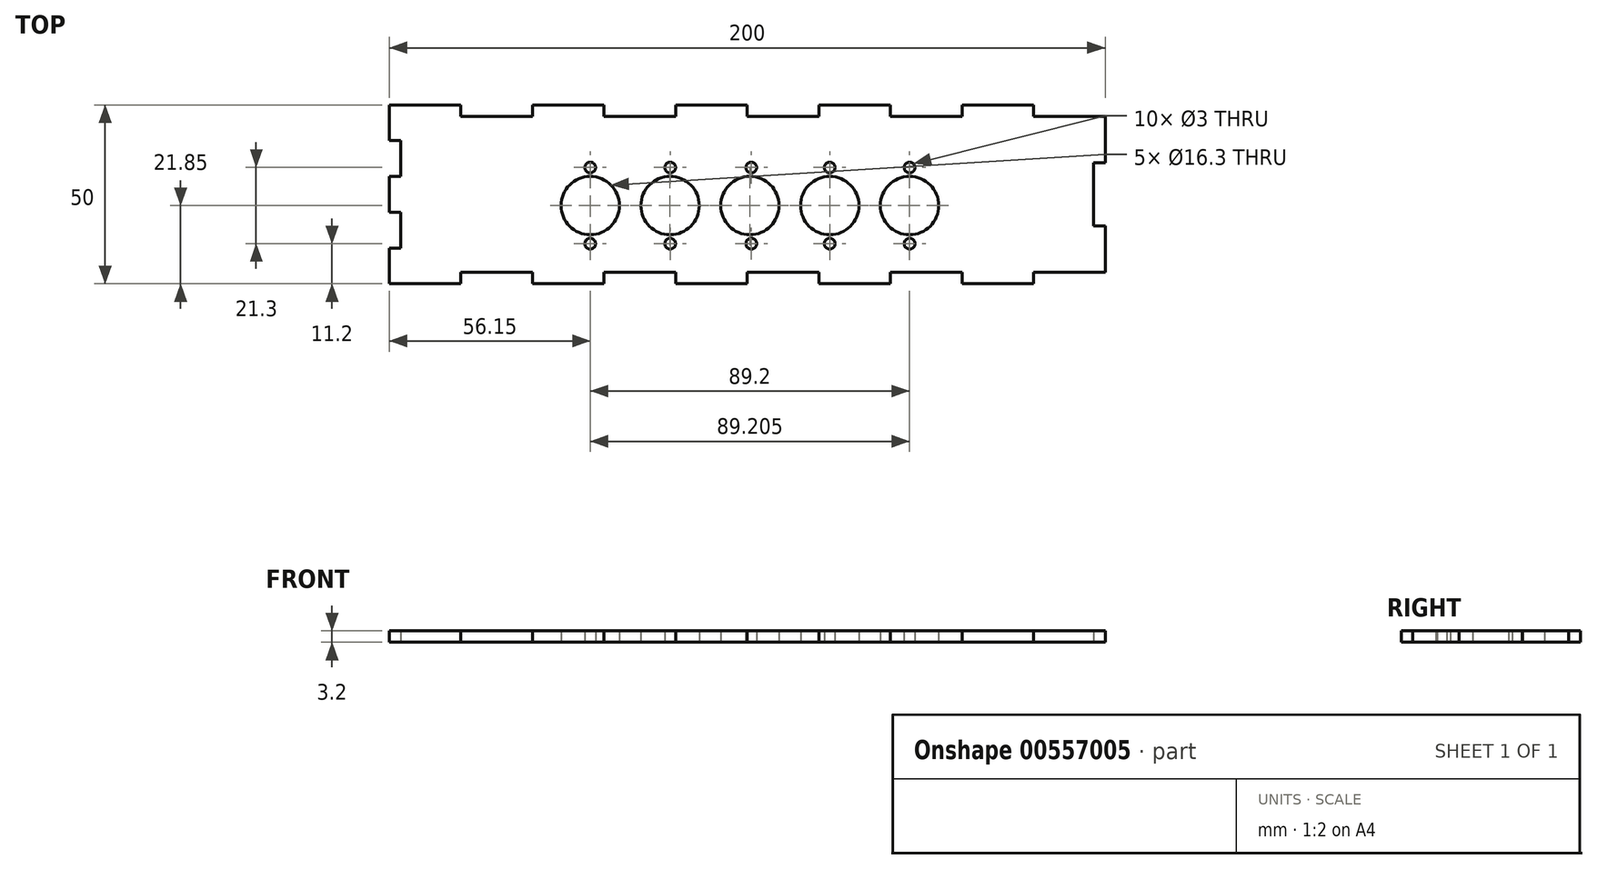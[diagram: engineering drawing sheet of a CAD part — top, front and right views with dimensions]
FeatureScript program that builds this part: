
annotation { "Feature Type Name" : "Feature", "Feature Type Description" : "" }
export const myFeature = defineFeature(function(context is Context, id is Id, definition is map)
    precondition{}
    {
        {
            var Q0;
            Q0=qCreatedBy(makeId("Top.planeOp"),FACE);
            var sketch = newSketch(context, id + "F0", { "sketchPlane" : qUnion([Q0])});
            skLineSegment(sketch, "E0.bottom", {"start": v(-60, 28.15) * mm, "end": v(-40, 28.15) * mm});
            skLineSegment(sketch, "E0.top", {"start": v(-60, -21.85) * mm, "end": v(-40, -21.85) * mm});
            skLineSegment(sketch, "E0.left", {"start": v(-60, 28.15) * mm, "end": v(-60, 18.15) * mm});
            skLineSegment(sketch, "E0.right", {"start": v(140, 24.95) * mm, "end": v(140, 11.95) * mm});
            skCircle(sketch, "E1", {"center": v(-3.85, 0) * mm, "radius": 8.15 * mm});
            skCircle(sketch, "E2", {"center": v(18.45, 0) * mm, "radius": 8.15 * mm});
            skCircle(sketch, "E3", {"center": v(40.75, 0) * mm, "radius": 8.15 * mm});
            skCircle(sketch, "E4", {"center": v(63.05, 0) * mm, "radius": 8.15 * mm});
            skCircle(sketch, "E5", {"center": v(85.35, 0) * mm, "radius": 8.15 * mm});
            skLineSegment(sketch, "E6.top", {"start": v(120, 24.95) * mm, "end": v(140, 24.95) * mm});
            skLineSegment(sketch, "E6.left", {"start": v(120, 28.15) * mm, "end": v(120, 24.95) * mm});
            skPoint(sketch, "E7.orphan", {"position": v(140, 28.15) * mm});
            skLineSegment(sketch, "E8.top", {"start": v(80, 24.95) * mm, "end": v(100, 24.95) * mm});
            skLineSegment(sketch, "E8.left", {"start": v(80, 28.15) * mm, "end": v(80, 24.95) * mm});
            skLineSegment(sketch, "E8.right", {"start": v(100, 28.15) * mm, "end": v(100, 24.95) * mm});
            skLineSegment(sketch, "E9.trimOffspring", {"start": v(100, 28.15) * mm, "end": v(120, 28.15) * mm});
            skLineSegment(sketch, "E10.top", {"start": v(40, 24.95) * mm, "end": v(60, 24.95) * mm});
            skLineSegment(sketch, "E10.left", {"start": v(40, 28.15) * mm, "end": v(40, 24.95) * mm});
            skLineSegment(sketch, "E10.right", {"start": v(60, 28.15) * mm, "end": v(60, 24.95) * mm});
            skLineSegment(sketch, "E11.trimOffspring", {"start": v(60, 28.15) * mm, "end": v(80, 28.15) * mm});
            skLineSegment(sketch, "E12.top", {"start": v(0, 24.95) * mm, "end": v(20, 24.95) * mm});
            skLineSegment(sketch, "E12.left", {"start": v(0, 28.15) * mm, "end": v(0, 24.95) * mm});
            skLineSegment(sketch, "E12.right", {"start": v(20, 28.15) * mm, "end": v(20, 24.95) * mm});
            skLineSegment(sketch, "E13.top", {"start": v(-40, 24.95) * mm, "end": v(-20, 24.95) * mm});
            skLineSegment(sketch, "E13.left", {"start": v(-40, 28.15) * mm, "end": v(-40, 24.95) * mm});
            skLineSegment(sketch, "E13.right", {"start": v(-20, 28.15) * mm, "end": v(-20, 24.95) * mm});
            skLineSegment(sketch, "E14.trimOffspring", {"start": v(20, 28.15) * mm, "end": v(40, 28.15) * mm});
            skLineSegment(sketch, "E15.trimOffspring", {"start": v(-20, 28.15) * mm, "end": v(0, 28.15) * mm});
            skLineSegment(sketch, "E16.bottom", {"start": v(-60, 18.15) * mm, "end": v(-56.8, 18.15) * mm});
            skLineSegment(sketch, "E16.top", {"start": v(-60, 8.15) * mm, "end": v(-56.8, 8.15) * mm});
            skLineSegment(sketch, "E16.right", {"start": v(-56.8, 18.15) * mm, "end": v(-56.8, 8.15) * mm});
            skPoint(sketch, "E17.oppositeSnap0", {"position": v(-56.8, 13.15) * mm});
            skLineSegment(sketch, "E18.bottom", {"start": v(-60, -1.85) * mm, "end": v(-56.8, -1.85) * mm});
            skLineSegment(sketch, "E18.top", {"start": v(-60, -11.85) * mm, "end": v(-56.8, -11.85) * mm});
            skLineSegment(sketch, "E18.right", {"start": v(-56.8, -1.85) * mm, "end": v(-56.8, -11.85) * mm});
            skLineSegment(sketch, "E19.trimOffspring", {"start": v(-60, 8.15) * mm, "end": v(-60, -1.85) * mm});
            skLineSegment(sketch, "E20.trimOffspring", {"start": v(-60, -11.85) * mm, "end": v(-60, -21.85) * mm});
            skLineSegment(sketch, "E21.bottom", {"start": v(-40, -18.65) * mm, "end": v(-20, -18.65) * mm});
            skLineSegment(sketch, "E21.left", {"start": v(-40, -18.65) * mm, "end": v(-40, -21.85) * mm});
            skLineSegment(sketch, "E21.right", {"start": v(-20, -18.65) * mm, "end": v(-20, -21.85) * mm});
            skLineSegment(sketch, "E22.bottom", {"start": v(0, -18.65) * mm, "end": v(20, -18.65) * mm});
            skLineSegment(sketch, "E22.left", {"start": v(0, -18.65) * mm, "end": v(0, -21.85) * mm});
            skLineSegment(sketch, "E22.right", {"start": v(20, -18.65) * mm, "end": v(20, -21.85) * mm});
            skLineSegment(sketch, "E23.bottom", {"start": v(40, -18.65) * mm, "end": v(60, -18.65) * mm});
            skLineSegment(sketch, "E23.left", {"start": v(40, -18.65) * mm, "end": v(40, -21.85) * mm});
            skLineSegment(sketch, "E23.right", {"start": v(60, -18.65) * mm, "end": v(60, -21.85) * mm});
            skLineSegment(sketch, "E24.bottom", {"start": v(80, -18.65) * mm, "end": v(100, -18.65) * mm});
            skLineSegment(sketch, "E24.left", {"start": v(80, -18.65) * mm, "end": v(80, -21.85) * mm});
            skLineSegment(sketch, "E24.right", {"start": v(100, -18.65) * mm, "end": v(100, -21.85) * mm});
            skLineSegment(sketch, "E25.bottom", {"start": v(120, -18.65) * mm, "end": v(140, -18.65) * mm});
            skLineSegment(sketch, "E25.left", {"start": v(120, -18.65) * mm, "end": v(120, -21.85) * mm});
            skLineSegment(sketch, "E25.right", {"start": v(140, -18.65) * mm, "end": v(140, -21.85) * mm});
            skLineSegment(sketch, "E26.trimOffspring", {"start": v(-20, -21.85) * mm, "end": v(0, -21.85) * mm});
            skLineSegment(sketch, "E27.trimOffspring", {"start": v(20, -21.85) * mm, "end": v(40, -21.85) * mm});
            skLineSegment(sketch, "E28.trimOffspring", {"start": v(60, -21.85) * mm, "end": v(80, -21.85) * mm});
            skLineSegment(sketch, "E29.trimOffspring", {"start": v(100, -21.85) * mm, "end": v(120, -21.85) * mm});
            skLineSegment(sketch, "E30.bottom", {"start": v(136.8, 11.95) * mm, "end": v(140, 11.95) * mm});
            skLineSegment(sketch, "E30.top", {"start": v(136.8, -5.65) * mm, "end": v(140, -5.65) * mm});
            skLineSegment(sketch, "E30.left", {"start": v(136.8, 11.95) * mm, "end": v(136.8, -5.65) * mm});
            skLineSegment(sketch, "E31.trimOffspring", {"start": v(140, -5.65) * mm, "end": v(140, -21.85) * mm});
            skLineSegment(sketch, "E32", {"start": v(85.36, 10.65) * mm, "end": v(85.36, -10.65) * mm});
            skCircle(sketch, "E33", {"center": v(85.36, 10.65) * mm, "radius": 1.5 * mm});
            skCircle(sketch, "E34", {"center": v(85.36, -10.65) * mm, "radius": 1.5 * mm});
            skLineSegment(sketch, "E35", {"start": v(63.05, 10.65) * mm, "end": v(63.05, -10.65) * mm});
            skCircle(sketch, "E36", {"center": v(63.05, 10.65) * mm, "radius": 1.5 * mm});
            skCircle(sketch, "E37", {"center": v(63.05, -10.65) * mm, "radius": 1.5 * mm});
            skLineSegment(sketch, "E38", {"start": v(41.13, 10.64) * mm, "end": v(41.13, -10.64) * mm});
            skCircle(sketch, "E39", {"center": v(41.13, 10.64) * mm, "radius": 1.5 * mm});
            skCircle(sketch, "E40", {"center": v(41.13, -10.64) * mm, "radius": 1.5 * mm});
            skLineSegment(sketch, "E41", {"start": v(18.5, 10.65) * mm, "end": v(18.5, -10.65) * mm});
            skCircle(sketch, "E42", {"center": v(18.5, 10.65) * mm, "radius": 1.5 * mm});
            skCircle(sketch, "E43", {"center": v(18.5, -10.65) * mm, "radius": 1.5 * mm});
            skLineSegment(sketch, "E44", {"start": v(-3.85, 10.65) * mm, "end": v(-3.85, -10.65) * mm});
            skCircle(sketch, "E45", {"center": v(-3.85, 10.65) * mm, "radius": 1.5 * mm});
            skCircle(sketch, "E46", {"center": v(-3.85, -10.65) * mm, "radius": 1.5 * mm});
            skSolve(sketch);
        }
        {
            var Q0;
            Q0=qSketchRegion(id+"F0",true);
            extrude(context, id + "F1", {"entities" : qUnion([Q0]), "depth" : 3.2 * mm});
        }
    });
